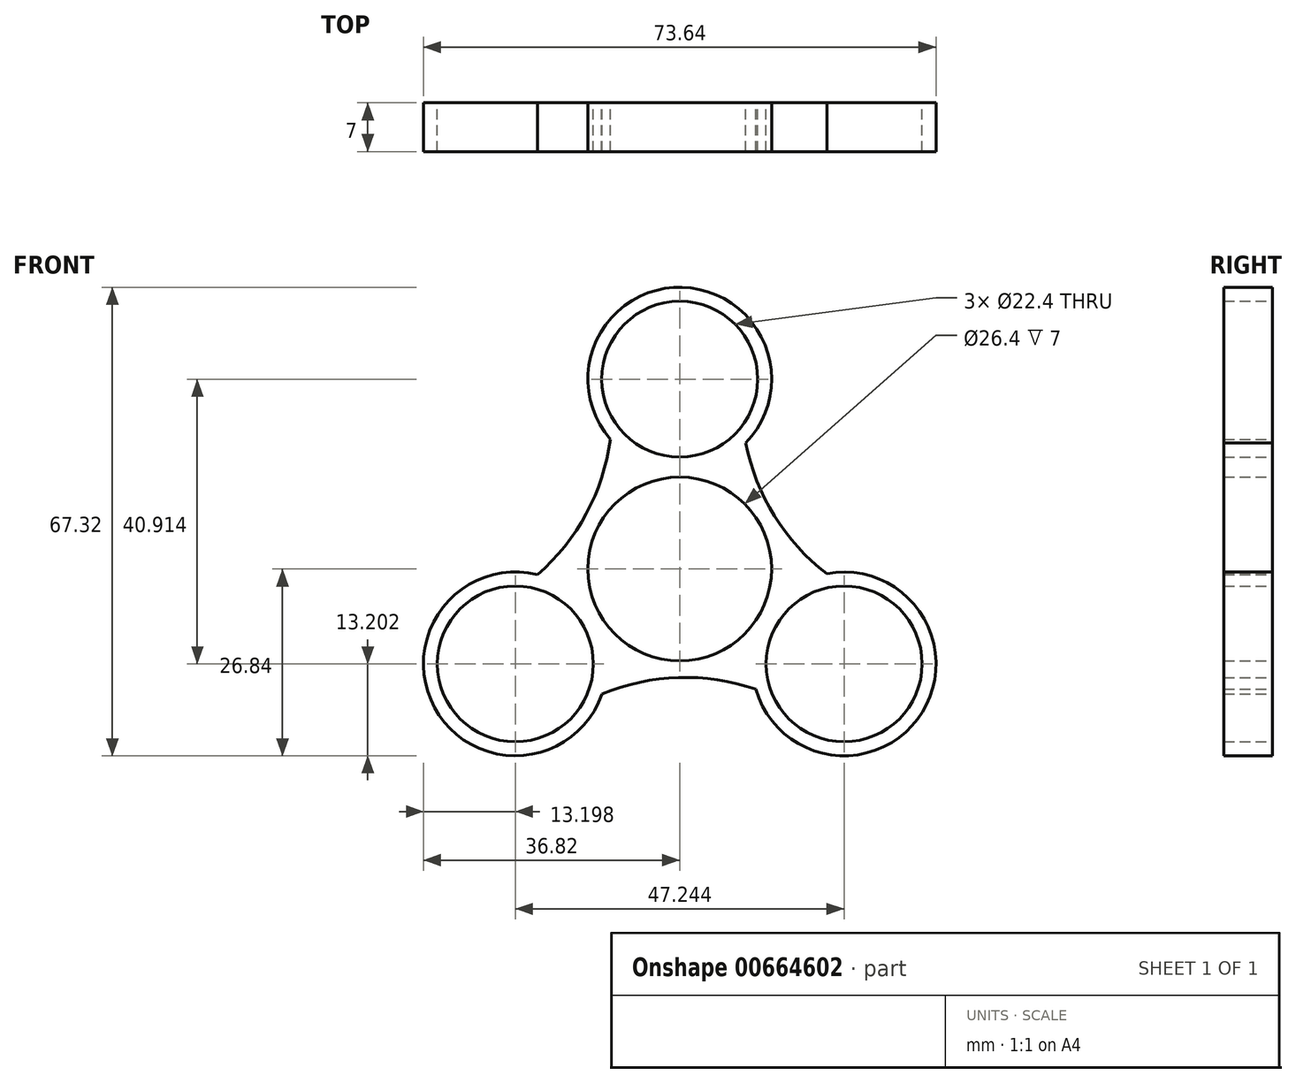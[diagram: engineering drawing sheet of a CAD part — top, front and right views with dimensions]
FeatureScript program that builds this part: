
annotation { "Feature Type Name" : "Feature", "Feature Type Description" : "" }
export const myFeature = defineFeature(function(context is Context, id is Id, definition is map)
    precondition{}
    {
        {
            var Q0;
            Q0=qCreatedBy(makeId("Front.planeOp"),FACE);
            var sketch = newSketch(context, id + "F0", { "sketchPlane" : qUnion([Q0])});
            skCircle(sketch, "E0", {"center": v(0, 0) * mm, "radius": 11.2 * mm});
            skCircle(sketch, "E1", {"center": v(0, 0) * mm, "radius": 13.2 * mm});
            skCircle(sketch, "E2", {"center": v(0, 27.28) * mm, "radius": 11.2 * mm});
            skArc(sketch, "E3", {"start": v(9.5, 18.11) * mm, "mid": v(0.36, 40.47) * mm, "end": v(-9.99, 18.64) * mm});
            skCircle(sketch, "E4.1.0", {"center": v(-23.62, -13.64) * mm, "radius": 11.2 * mm});
            skArc(sketch, "E4.1.1", {"start": v(-20.44, -0.83) * mm, "mid": v(-35.23, -19.93) * mm, "end": v(-11.15, -17.97) * mm});
            skCircle(sketch, "E4.2.0", {"center": v(23.62, -13.64) * mm, "radius": 11.2 * mm});
            skArc(sketch, "E4.2.1", {"start": v(10.94, -17.29) * mm, "mid": v(34.87, -20.55) * mm, "end": v(21.14, -0.67) * mm});
            skArc(sketch, "E5", {"start": v(10.94, -17.29) * mm, "mid": v(-0.17, -15.6) * mm, "end": v(-11.15, -17.97) * mm});
            skArc(sketch, "E6.1.0", {"start": v(9.5, 18.11) * mm, "mid": v(13.6, 7.65) * mm, "end": v(21.14, -0.67) * mm});
            skArc(sketch, "E6.2.0", {"start": v(-20.44, -0.83) * mm, "mid": v(-13.42, 7.95) * mm, "end": v(-9.99, 18.64) * mm});
            skSolve(sketch);
        }
        {
            var Q0;
            Q0 = qSketchRegion(id + "F0", true);
            extrude(context, id + "F1", {"entities" : qUnion([Q0]), "depth" : 7 * mm, "offsetDistance" : 25 * mm});
        }
    });
